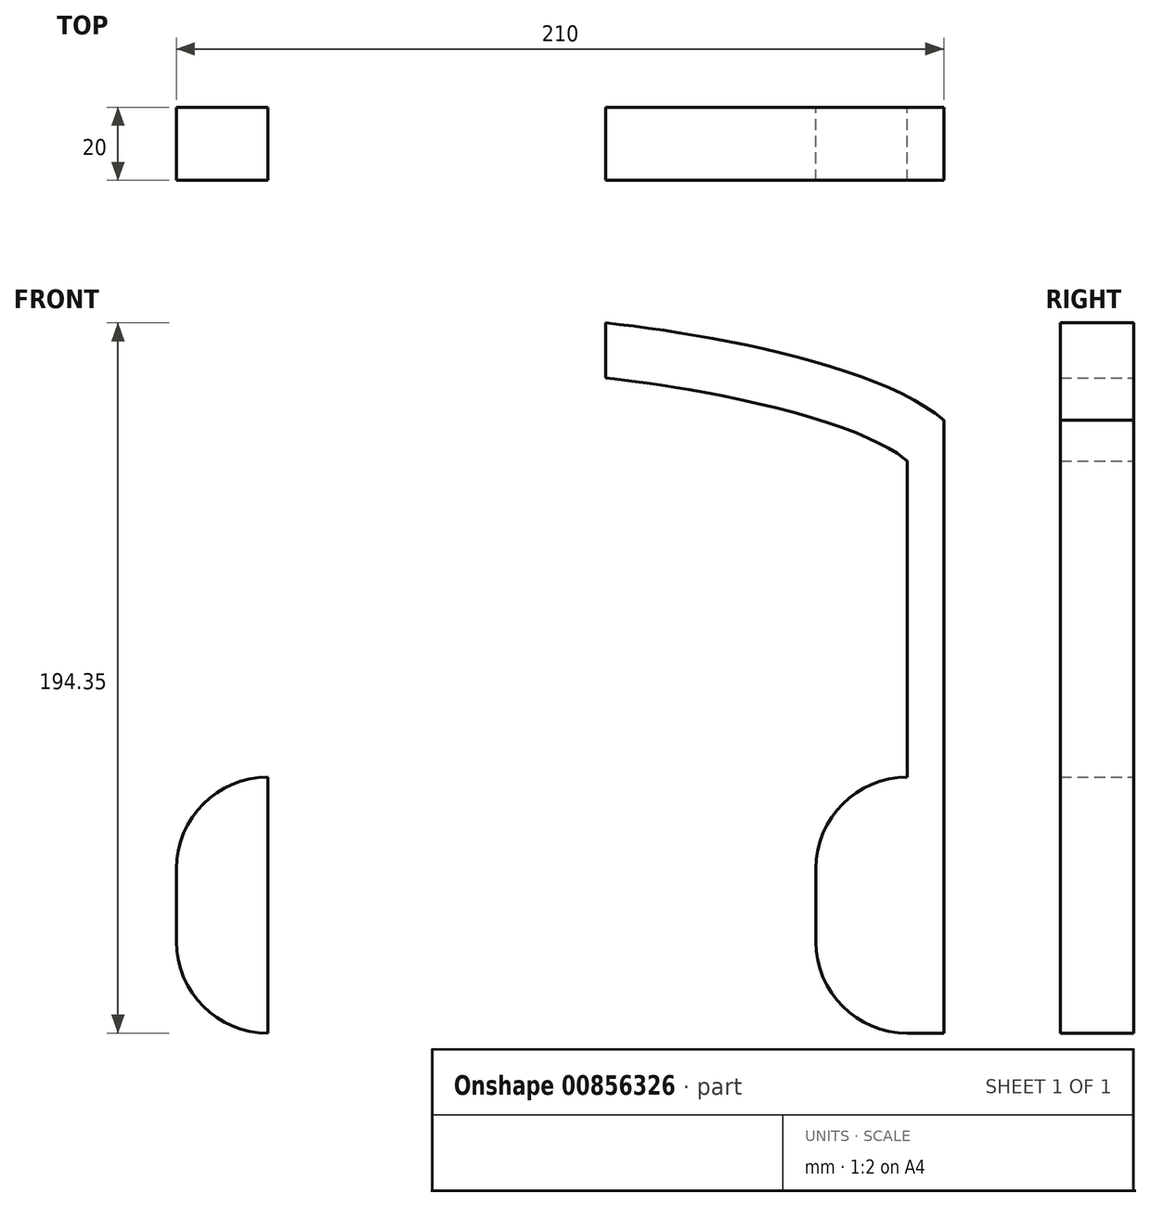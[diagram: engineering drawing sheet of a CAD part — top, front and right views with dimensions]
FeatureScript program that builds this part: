
annotation { "Feature Type Name" : "Feature", "Feature Type Description" : "" }
export const myFeature = defineFeature(function(context is Context, id is Id, definition is map)
    precondition{}
    {
        {
            var Q0;
            Q0=qCreatedBy(makeId("Front.planeOp"),FACE);
            var sketch = newSketch(context, id + "F0", { "sketchPlane" : qUnion([Q0])});
            skLineSegment(sketch, "E0.bottom", {"start": v(0, 0) * mm, "end": v(185, 0) * mm});
            skLineSegment(sketch, "E0.top", {"start": v(0, 200) * mm, "end": v(185, 200) * mm});
            skLineSegment(sketch, "E0.left", {"start": v(0, 0) * mm, "end": v(0, 200) * mm});
            skLineSegment(sketch, "E0.right", {"start": v(185, 0) * mm, "end": v(185, 200) * mm});
            skFitSpline(sketch, "E1", {"points": [v(0, 174.13) * mm, v(92.5, 200) * mm, v(185, 173.31) * mm], "startDerivative": vector(355.54, 155.3) * mm, "endDerivative": vector(101.13, -90.45) * mm});
            skFitSpline(sketch, "E2.0", {"points": [v(6, 160.38) * mm, v(13.42, 163.62) * mm, v(26.55, 169.37) * mm, v(41.96, 175.96) * mm, v(51.86, 179.89) * mm, v(58.34, 182.18) * mm, v(62.57, 183.52) * mm, v(66.27, 184.5) * mm, v(69.57, 185.18) * mm, v(72.63, 185.62) * mm, v(75.65, 185.87) * mm, v(78.83, 185.93) * mm, v(82.33, 185.83) * mm, v(85.64, 185.6) * mm, v(88.58, 185.33) * mm, v(90.93, 185.09) * mm, v(93.43, 184.8) * mm, v(96.92, 184.4) * mm, v(101.55, 183.8) * mm, v(107.44, 182.94) * mm, v(115.63, 181.62) * mm, v(126.3, 179.64) * mm, v(139.13, 176.75) * mm, v(151.27, 173.37) * mm, v(160.21, 170.2) * mm, v(166.24, 167.57) * mm, v(170.07, 165.59) * mm, v(173.1, 163.7) * mm, v(174.48, 162.6) * mm, v(175, 162.13) * mm]});
            skLineSegment(sketch, "E3", {"start": v(92.5, 200) * mm, "end": v(92.5, 44.07) * mm});
            skLineSegment(sketch, "E4", {"start": v(0, 174.13) * mm, "end": v(0, 75.65) * mm});
            skLineSegment(sketch, "E5", {"start": v(0, 75.65) * mm, "end": v(10, 75.65) * mm});
            skLineSegment(sketch, "E6", {"start": v(10, 75.65) * mm, "end": v(10, 162.13) * mm});
            skLineSegment(sketch, "E7.bottom", {"start": v(10, 75.65) * mm, "end": v(0, 75.65) * mm});
            skLineSegment(sketch, "E7.top", {"start": v(10, 5.65) * mm, "end": v(0, 5.65) * mm});
            skLineSegment(sketch, "E7.left", {"start": v(35, 50.65) * mm, "end": v(35, 30.65) * mm});
            skLineSegment(sketch, "E7.right", {"start": v(-25, 50.65) * mm, "end": v(-25, 30.65) * mm});
            skPoint(sketch, "E8.visualSharp", {"position": v(35, 75.65) * mm});
            skArc(sketch, "E8.filletArc", {"start": v(35, 50.65) * mm, "mid": v(27.68, 68.33) * mm, "end": v(10, 75.65) * mm});
            skPoint(sketch, "E9.visualSharp", {"position": v(35, 5.65) * mm});
            skArc(sketch, "E9.filletArc", {"start": v(10, 5.65) * mm, "mid": v(27.68, 12.98) * mm, "end": v(35, 30.65) * mm});
            skPoint(sketch, "E10.visualSharp", {"position": v(-25, 5.65) * mm});
            skArc(sketch, "E10.filletArc", {"start": v(-25, 30.65) * mm, "mid": v(-17.68, 12.98) * mm, "end": v(0, 5.65) * mm});
            skPoint(sketch, "E11.visualSharp", {"position": v(-25, 75.65) * mm});
            skArc(sketch, "E11.filletArc", {"start": v(0, 75.65) * mm, "mid": v(-17.68, 68.33) * mm, "end": v(-25, 50.65) * mm});
            skLineSegment(sketch, "E12.MirrorCS", {"start": v(175, 75.65) * mm, "end": v(175, 162.13) * mm});
            skLineSegment(sketch, "E13.MirrorCS", {"start": v(185, 174.13) * mm, "end": v(185, 75.65) * mm});
            skArc(sketch, "E14.MirrorCS", {"start": v(185, 75.65) * mm, "mid": v(202.68, 68.33) * mm, "end": v(210, 50.65) * mm});
            skLineSegment(sketch, "E15.MirrorCS", {"start": v(175, 75.65) * mm, "end": v(185, 75.65) * mm});
            skArc(sketch, "E16.MirrorCS", {"start": v(150, 50.65) * mm, "mid": v(157.32, 68.33) * mm, "end": v(175, 75.65) * mm});
            skLineSegment(sketch, "E17.MirrorCS", {"start": v(150, 50.65) * mm, "end": v(150, 30.65) * mm});
            skArc(sketch, "E18.MirrorCS", {"start": v(175, 5.65) * mm, "mid": v(157.32, 12.98) * mm, "end": v(150, 30.65) * mm});
            skLineSegment(sketch, "E19.MirrorCS", {"start": v(175, 5.65) * mm, "end": v(185, 5.65) * mm});
            skArc(sketch, "E20.MirrorCS", {"start": v(210, 30.65) * mm, "mid": v(202.68, 12.98) * mm, "end": v(185, 5.65) * mm});
            skLineSegment(sketch, "E21.MirrorCS", {"start": v(210, 50.65) * mm, "end": v(210, 30.65) * mm});
            skSolve(sketch);
        }
        {
            var Q0;
            {var subQ1=sQuery(id+"F0.wireOp",EDGE,"E7.bottom");Q0=makeQuery(id+"F0.imprint","IMPRINT",FACE,{"disambiguationData":[TD([[makeQuery(id+"F0.imprint","IMPRINT",EDGE,{"derivedFrom":subQ1}),1.0]])]});}
            var Q1;
            Q1=makeQuery(id+"F0.imprint","IMPRINT",FACE,{"disambiguationData":[TD([[makeQuery(id+"F0.imprint","IMPRINT",EDGE,{"derivedFrom":sQuery(id+"F0.wireOp",EDGE,"E7.right")}),1.0]])]});
            var Q2;
            {var subQ8=sQuery(id+"F0.wireOp",EDGE,"E4");Q2=makeQuery(id+"F0.imprint","IMPRINT",FACE,{"disambiguationData":[TD([[makeQuery(id+"F0.imprint","IMPRINT",EDGE,{"derivedFrom":subQ8}),1.0]])]});}
            var Q3;
            Q3=makeQuery(id+"F0.imprint","IMPRINT",FACE,{"disambiguationData":[TD([[makeQuery(id+"F0.imprint","IMPRINT",EDGE,{"derivedFrom":sQuery(id+"F0.wireOp",EDGE,"E15.MirrorCS")}),1.0]])]});
            var Q4;
            {var subQ0=sQuery(id+"F0.wireOp",EDGE,"E14.MirrorCS");Q4=makeQuery(id+"F0.imprint","IMPRINT",FACE,{"disambiguationData":[TD([[makeQuery(id+"F0.imprint","IMPRINT",EDGE,{"derivedFrom":subQ0}),-1.0]])]});}
            var Q5;
            {var subQ0=sQuery(id+"F0.wireOp",EDGE,"E15.MirrorCS");Q5=makeQuery(id+"F0.imprint","IMPRINT",FACE,{"disambiguationData":[TD([[makeQuery(id+"F0.imprint","IMPRINT",EDGE,{"derivedFrom":subQ0}),-1.0]])]});}
            extrude(context, id + "F1", {"entities" : qUnion([Q0, Q1, Q2, Q3, Q4, Q5]), "depth" : 20 * mm, "offsetDistance" : 25 * mm});
        }
    });
